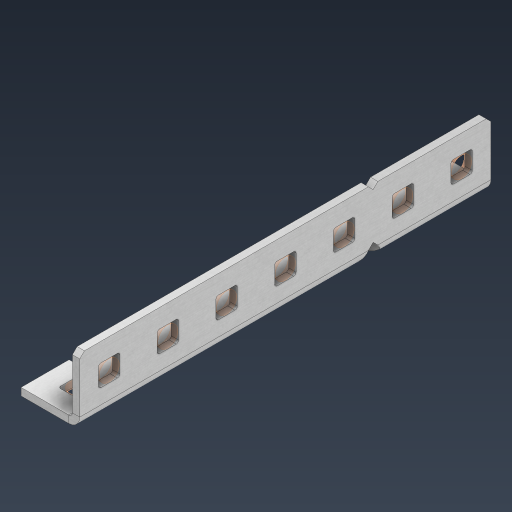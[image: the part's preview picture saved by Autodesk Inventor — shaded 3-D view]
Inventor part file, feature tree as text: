
AUTODESK INVENTOR PART (.ipt)
format: ipt  version: 2024.3 (Build 283343000, 343)  size: 531,456 bytes
history: native  units: in
note: dims shown in document units (in); Inventor stores cm internally (conversion verified against a paired STEP export)
features: other x28, extrude x19, sheet_metal_op x11, pattern_linear x2, mirror x1, chamfer x1, sketch x1
ambient origin geometry x8: Origin, YZ Plane, XZ Plane, XY Plane, X Axis, Y Axis, Z Axis, Center Point
bodies: Solid1 (feature_tree), Body (feature_tree)
feature tree (63):
  sheet_metal_op  "Flanges"
  other  "Flange Pattern Plane"
  other  "Flange Pattern Sketch"
  sheet_metal_op  "Flange Pattern"
  sheet_metal_op  "Body Pattern"
  pattern_linear  "Center Pattern"  Spacing1=3.5in  [1 undecoded]
  other  "Arc Length"
  mirror  "Notch Mirror"
  pattern_linear  "Notch Pattern"  Spacing1=0.0625in  [1 undecoded]
  chamfer  "End Chamfer"
  extrude  "Half Cut"  Depth=0.0625in
  other  "Plate1"
  sketch  "Sketch2"  dims[d0=1.0in d1=3.5in d2=0.0625in d3=0.0625in d4=0.0312in d5=0.125in d6=0.0625in d7=0.5in d8=90.0deg d9=0.0312in d10=0.25in d11=0.0625in d12=0.0625in d16=0.182in d17=0.02in d18=0.0625in d19=0.0in d20=0.25in d21=0.25in d38=2.7559in d40=0.5in d41=0.3937in d43=1.0in d46=0.172in d47=1.0in d48=0.0in d49=0.182in d50=0.02in d51=0.25in d52=0.25in d53=0.0625in d54=0.0in d55=0.172in d56=1.0in d57=0.0in d58=0.25in d60=2.7559in d62=0.5in d63=0.3937in d65=0.5in d85=0.1473in d86=0.1782in d88=0.04in d89=0.0625in d90=0.0in d91=0.04in d92=0.0491in d95=2.5in d96=0.04in d97=0.25in d98=45.0deg d99=0.25in d100=0.5in d101=0.0in d102=2.497in d106=0.182in d107=0.02in d108=0.5in d109=0.5in d110=0.0625in d111=0.0in d112=0.172in d113=0.5in d114=0.0in d117=0.5in d118=0.5in d119=0.5in]
  other  "Plate2"
  sheet_metal_op  "Bend1"
  sheet_metal_op  "Corner1"
  other  "Srf1"
  other  "Srf2"
  other  "Srf91"
  sheet_metal_op  "Body Pattern Sketch"
  other  "Srf92"
  other  "Srf786"
  other  "Srf823"
  other  "Srf824"
  other  "Srf825"
  other  "Srf826"
  other  "Srf827"
  other  "Srf856"
  other  "Srf857"
  other  "Srf858"
  other  "Srf859"
  other  "Srf860"
  other  "Srf889"
  other  "Srf890"
  other  "Srf891"
  other  "Srf892"
  other  "Srf893"
  other  "Srf894"
  sheet_metal_op  "Flange Stamp"
  sheet_metal_op  "Flange Circle"
  sheet_metal_op  "Body Stamp"
  sheet_metal_op  "Body Circle"
  other  "Center Stamp"
  other  "Center Circle"
  sheet_metal_op  "Notch"
  extrude  "ExtrusionSrf2"  Depth=0.0312in
  extrude  "ExtrusionSrf92"  Depth=0.5in
  extrude  "ExtrusionSrf823"  Depth=0.0625in
  extrude  "ExtrusionSrf824"  Depth=0.5in TaperAngle=90.0deg
  extrude  "ExtrusionSrf825"  Depth=0.5in
  extrude  "ExtrusionSrf826"  Depth=0.0625in
  extrude  "ExtrusionSrf827"  Depth=0.0625in
  extrude  "ExtrusionSrf856"  Depth=0.182in
  extrude  "ExtrusionSrf857"  Depth=0.02in
  extrude  "ExtrusionSrf858"  Depth=0.0625in
  extrude  "ExtrusionSrf859"  TaperAngle=0.0deg  [1 undecoded]
  extrude  "ExtrusionSrf860"  Depth=0.5in
  extrude  "ExtrusionSrf889"  Depth=0.5in
  extrude  "ExtrusionSrf890"  Depth=0.5in
  extrude  "ExtrusionSrf891"  Depth=0.5in
  extrude  "ExtrusionSrf892"  Depth=1.0in TaperAngle=0.0deg
  extrude  "ExtrusionSrf893"  Depth=0.182in
  extrude  "ExtrusionSrf894"  Depth=0.02in
note: 3 required parameter values undecoded (feature->parameter linkage not recoverable at this tier; creation-order binding heuristic only, values carry confidence <= 0.55)
